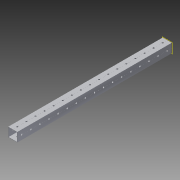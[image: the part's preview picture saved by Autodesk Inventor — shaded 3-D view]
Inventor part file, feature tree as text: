
AUTODESK INVENTOR PART (.ipt)
format: ipt  version: 2014 (Build 180170000, 170)  size: 1,248,768 bytes
history: native  units: in
note: dims shown in document units (in); Inventor stores cm internally (conversion verified against a paired STEP export)
features: pattern_circular x1, other x1, plane x1, extrude x1, imported_body x1, sketch x1
ambient origin geometry x8: Origin, YZ Plane, XZ Plane, XY Plane, X Axis, Y Axis, Z Axis, Center Point
bodies: Body1 (feature_tree)
feature tree (6):
  pattern_circular  "CirPattern2"
  other  "217-3426-STEP1"
  plane  "Work Plane1"
  extrude  "Extrusion1"  Depth=3937.0079in TaperAngle=0.0deg
  imported_body  "Base1"
  sketch  "Sketch1"  dims[d0=-17.0in d1=3937.0079in d2=0.0in]
